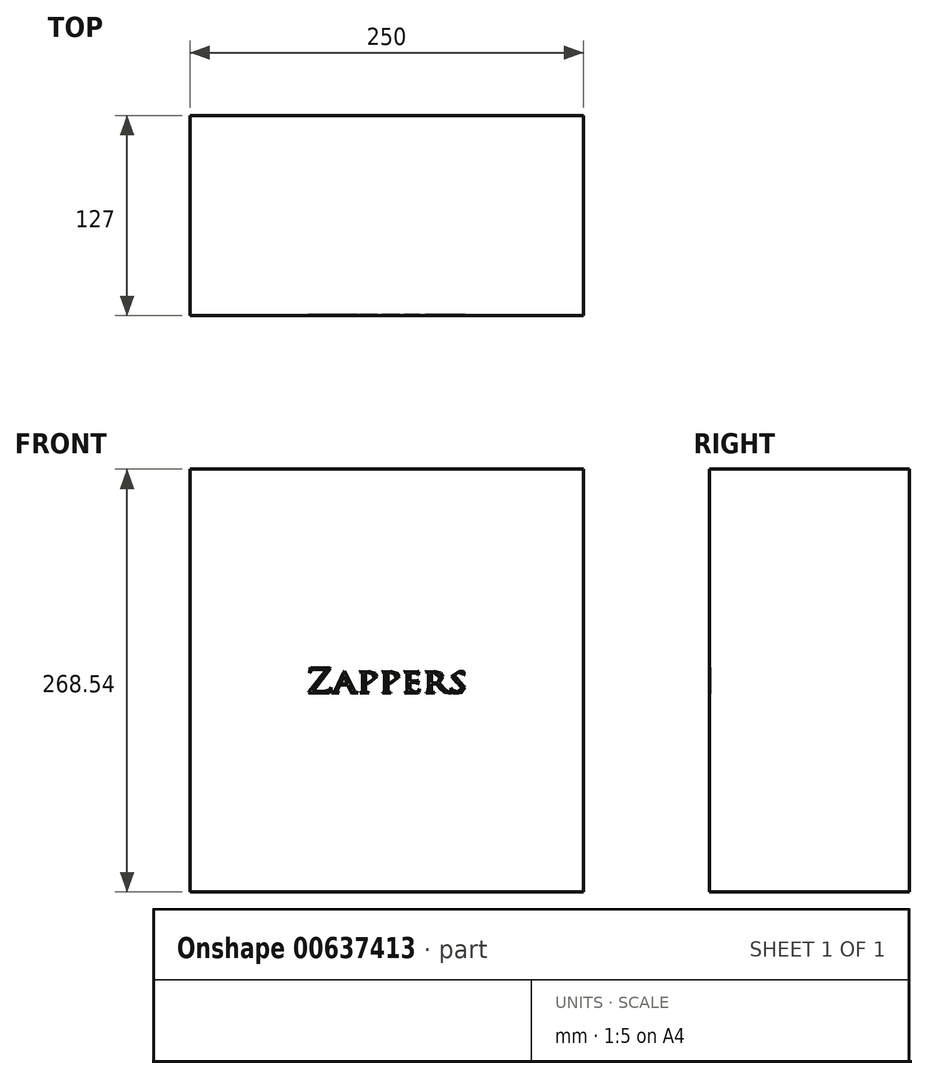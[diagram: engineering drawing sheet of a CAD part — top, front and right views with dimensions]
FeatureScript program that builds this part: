
annotation { "Feature Type Name" : "Feature", "Feature Type Description" : "" }
export const myFeature = defineFeature(function(context is Context, id is Id, definition is map)
    precondition{}
    {
        {
            var Q0;
            Q0=qCreatedBy(makeId("Front.planeOp"),FACE);
            var sketch = newSketch(context, id + "F0", { "sketchPlane" : qUnion([Q0])});
            skLineSegment(sketch, "E0.bottom", {"start": v(125, 134.27) * mm, "end": v(-125, 134.27) * mm});
            skLineSegment(sketch, "E0.top", {"start": v(125, -134.27) * mm, "end": v(-125, -134.27) * mm});
            skLineSegment(sketch, "E0.left", {"start": v(125, 134.27) * mm, "end": v(125, -134.27) * mm});
            skLineSegment(sketch, "E0.right", {"start": v(-125, 134.27) * mm, "end": v(-125, -134.27) * mm});
            skPoint(sketch, "E0.middle", {"position": v(0, 0) * mm});
            skSolve(sketch);
        }
        {
            var Q0;
            Q0=makeQuery(id+"F0.imprint","IMPRINT",FACE,{"disambiguationData":[TD([[makeQuery(id+"F0.imprint","IMPRINT",EDGE,{"derivedFrom":sQuery(id+"F0.wireOp",EDGE,"E0.bottom")}),1.0]])]});
            extrude(context, id + "F1", {"entities" : qUnion([Q0]), "endBound" : BoundingType.SYMMETRIC, "depth" : 127 * mm, "offsetDistance" : 25.4 * mm, "hasSecondDirection" : true, "secondDirectionOppositeDirection" : true, "secondDirectionDepth" : 25.4 * mm});
        }
        {
            var Q0;
            Q0=makeQuery(id+"F1.opExtrude","CAP_FACE",FACE,{"disambiguationData":[OSD([sQuery(id+"F0.wireOp",EDGE,"E0.bottom"),sQuery(id+"F0.wireOp",EDGE,"E0.top"),sQuery(id+"F0.wireOp",EDGE,"E0.left"),sQuery(id+"F0.wireOp",EDGE,"E0.right")])],"isStart":false});
            var sketch = newSketch(context, id + "F2", { "sketchPlane" : qUnion([Q0])});
            skLineSegment(sketch, "E1", {"start": v(-40.14, -7) * mm, "end": v(-36.24, -5.97) * mm});
            skLineSegment(sketch, "E2", {"start": v(-36.24, -5.97) * mm, "end": v(-35.75, -4.84) * mm});
            skLineSegment(sketch, "E3", {"start": v(-35.75, -4.84) * mm, "end": v(-35.53, -4.5) * mm});
            skLineSegment(sketch, "E4", {"start": v(-35.53, -4.5) * mm, "end": v(-35.33, -4.98) * mm});
            skLineSegment(sketch, "E5", {"start": v(-35.33, -4.98) * mm, "end": v(-35.82, -7.4) * mm});
            skLineSegment(sketch, "E6", {"start": v(-35.82, -7.4) * mm, "end": v(-36.56, -7.95) * mm});
            skLineSegment(sketch, "E7", {"start": v(-36.56, -7.95) * mm, "end": v(-49.14, -7.84) * mm});
            skLineSegment(sketch, "E8", {"start": v(-49.14, -7.84) * mm, "end": v(-49.58, -7.67) * mm});
            skLineSegment(sketch, "E9", {"start": v(-49.58, -7.67) * mm, "end": v(-49.24, -7.09) * mm});
            skLineSegment(sketch, "E10", {"start": v(-49.24, -7.09) * mm, "end": v(-38.41, 7.13) * mm});
            skLineSegment(sketch, "E11", {"start": v(-38.41, 7.13) * mm, "end": v(-43.76, 7.13) * mm});
            skLineSegment(sketch, "E12", {"start": v(-43.76, 7.13) * mm, "end": v(-47.32, 6.7) * mm});
            skLineSegment(sketch, "E13", {"start": v(-47.32, 6.7) * mm, "end": v(-48.72, 5.05) * mm});
            skLineSegment(sketch, "E14", {"start": v(-48.72, 5.05) * mm, "end": v(-49, 4.67) * mm});
            skLineSegment(sketch, "E15", {"start": v(-49, 4.67) * mm, "end": v(-49.14, 4.94) * mm});
            skLineSegment(sketch, "E16", {"start": v(-49.14, 4.94) * mm, "end": v(-48.65, 7.74) * mm});
            skLineSegment(sketch, "E17", {"start": v(-48.65, 7.74) * mm, "end": v(-48.4, 8.14) * mm});
            skLineSegment(sketch, "E18", {"start": v(-48.4, 8.14) * mm, "end": v(-47.36, 7.99) * mm});
            skLineSegment(sketch, "E19", {"start": v(-47.36, 7.99) * mm, "end": v(-43.07, 7.93) * mm});
            skLineSegment(sketch, "E20", {"start": v(-43.07, 7.93) * mm, "end": v(-36.2, 7.93) * mm});
            skLineSegment(sketch, "E21", {"start": v(-36.2, 7.93) * mm, "end": v(-35.7, 7.76) * mm});
            skLineSegment(sketch, "E22", {"start": v(-35.7, 7.76) * mm, "end": v(-35.8, 7.5) * mm});
            skLineSegment(sketch, "E23", {"start": v(-35.8, 7.5) * mm, "end": v(-46.85, -7) * mm});
            skLineSegment(sketch, "E24", {"start": v(-46.85, -7) * mm, "end": v(-40.14, -7) * mm});
            skLineSegment(sketch, "E25", {"start": v(-27.46, 5.26) * mm, "end": v(-26.94, 5.95) * mm});
            skLineSegment(sketch, "E26", {"start": v(-26.94, 5.95) * mm, "end": v(-26.43, 5.3) * mm});
            skLineSegment(sketch, "E27", {"start": v(-26.43, 5.3) * mm, "end": v(-21.22, -5.55) * mm});
            skLineSegment(sketch, "E28", {"start": v(-21.22, -5.55) * mm, "end": v(-19.37, -7.5) * mm});
            skLineSegment(sketch, "E29", {"start": v(-19.37, -7.5) * mm, "end": v(-18.5, -7.61) * mm});
            skLineSegment(sketch, "E30", {"start": v(-18.5, -7.61) * mm, "end": v(-18.24, -7.76) * mm});
            skLineSegment(sketch, "E31", {"start": v(-18.24, -7.76) * mm, "end": v(-18.73, -7.9) * mm});
            skLineSegment(sketch, "E32", {"start": v(-18.73, -7.9) * mm, "end": v(-22.16, -7.86) * mm});
            skLineSegment(sketch, "E33", {"start": v(-22.16, -7.86) * mm, "end": v(-22.92, -7.74) * mm});
            skLineSegment(sketch, "E34", {"start": v(-22.92, -7.74) * mm, "end": v(-22.78, -7.61) * mm});
            skLineSegment(sketch, "E35", {"start": v(-22.78, -7.61) * mm, "end": v(-22.58, -7.13) * mm});
            skLineSegment(sketch, "E36", {"start": v(-22.58, -7.13) * mm, "end": v(-24.53, -3.03) * mm});
            skLineSegment(sketch, "E37", {"start": v(-24.53, -3.03) * mm, "end": v(-24.72, -2.92) * mm});
            skLineSegment(sketch, "E38", {"start": v(-24.72, -2.92) * mm, "end": v(-29.73, -2.92) * mm});
            skLineSegment(sketch, "E39", {"start": v(-29.73, -2.92) * mm, "end": v(-29.95, -3.07) * mm});
            skLineSegment(sketch, "E40", {"start": v(-29.95, -3.07) * mm, "end": v(-31.19, -5.93) * mm});
            skLineSegment(sketch, "E41", {"start": v(-31.19, -5.93) * mm, "end": v(-31.5, -7.13) * mm});
            skLineSegment(sketch, "E42", {"start": v(-31.5, -7.13) * mm, "end": v(-30.77, -7.61) * mm});
            skLineSegment(sketch, "E43", {"start": v(-30.77, -7.61) * mm, "end": v(-30.57, -7.61) * mm});
            skLineSegment(sketch, "E44", {"start": v(-30.57, -7.61) * mm, "end": v(-30.35, -7.76) * mm});
            skLineSegment(sketch, "E45", {"start": v(-30.35, -7.76) * mm, "end": v(-30.67, -7.9) * mm});
            skLineSegment(sketch, "E46", {"start": v(-30.67, -7.9) * mm, "end": v(-32.62, -7.84) * mm});
            skLineSegment(sketch, "E47", {"start": v(-32.62, -7.84) * mm, "end": v(-34.81, -7.9) * mm});
            skLineSegment(sketch, "E48", {"start": v(-34.81, -7.9) * mm, "end": v(-35.23, -7.76) * mm});
            skLineSegment(sketch, "E49", {"start": v(-35.23, -7.76) * mm, "end": v(-35.03, -7.61) * mm});
            skLineSegment(sketch, "E50", {"start": v(-35.03, -7.61) * mm, "end": v(-34.4, -7.57) * mm});
            skLineSegment(sketch, "E51", {"start": v(-34.4, -7.57) * mm, "end": v(-32.57, -5.93) * mm});
            skLineSegment(sketch, "E52", {"start": v(-32.57, -5.93) * mm, "end": v(-27.46, 5.26) * mm});
            skLineSegment(sketch, "E53", {"start": v(-25.04, -2.19) * mm, "end": v(-24.97, -2.06) * mm});
            skLineSegment(sketch, "E54", {"start": v(-24.97, -2.06) * mm, "end": v(-27.12, 2.84) * mm});
            skLineSegment(sketch, "E55", {"start": v(-27.12, 2.84) * mm, "end": v(-27.49, 2.84) * mm});
            skLineSegment(sketch, "E56", {"start": v(-27.49, 2.84) * mm, "end": v(-29.5, -2.06) * mm});
            skLineSegment(sketch, "E57", {"start": v(-29.5, -2.06) * mm, "end": v(-29.43, -2.19) * mm});
            skLineSegment(sketch, "E58", {"start": v(-29.43, -2.19) * mm, "end": v(-25.04, -2.19) * mm});
            skLineSegment(sketch, "E59", {"start": v(-15.38, 0.44) * mm, "end": v(-15.43, 4.29) * mm});
            skLineSegment(sketch, "E60", {"start": v(-15.43, 4.29) * mm, "end": v(-16.31, 5.28) * mm});
            skLineSegment(sketch, "E61", {"start": v(-16.31, 5.28) * mm, "end": v(-17.05, 5.32) * mm});
            skLineSegment(sketch, "E62", {"start": v(-17.05, 5.32) * mm, "end": v(-17.23, 5.47) * mm});
            skLineSegment(sketch, "E63", {"start": v(-17.23, 5.47) * mm, "end": v(-16.88, 5.61) * mm});
            skLineSegment(sketch, "E64", {"start": v(-16.88, 5.61) * mm, "end": v(-14.37, 5.57) * mm});
            skLineSegment(sketch, "E65", {"start": v(-14.37, 5.57) * mm, "end": v(-11.28, 5.61) * mm});
            skLineSegment(sketch, "E66", {"start": v(-11.28, 5.61) * mm, "end": v(-7.14, 4.6) * mm});
            skLineSegment(sketch, "E67", {"start": v(-7.14, 4.6) * mm, "end": v(-6.05, 2.46) * mm});
            skLineSegment(sketch, "E68", {"start": v(-6.05, 2.46) * mm, "end": v(-11.65, -1.8) * mm});
            skLineSegment(sketch, "E69", {"start": v(-11.65, -1.8) * mm, "end": v(-12.27, -1.79) * mm});
            skLineSegment(sketch, "E70", {"start": v(-12.27, -1.79) * mm, "end": v(-12.5, -1.62) * mm});
            skLineSegment(sketch, "E71", {"start": v(-12.5, -1.62) * mm, "end": v(-11.92, -1.43) * mm});
            skLineSegment(sketch, "E72", {"start": v(-11.92, -1.43) * mm, "end": v(-7.9, 1.45) * mm});
            skLineSegment(sketch, "E73", {"start": v(-7.9, 1.45) * mm, "end": v(-9.14, 4.16) * mm});
            skLineSegment(sketch, "E74", {"start": v(-9.14, 4.16) * mm, "end": v(-12.07, 5.03) * mm});
            skLineSegment(sketch, "E75", {"start": v(-12.07, 5.03) * mm, "end": v(-13.28, 4.9) * mm});
            skLineSegment(sketch, "E76", {"start": v(-13.28, 4.9) * mm, "end": v(-13.45, 4.56) * mm});
            skLineSegment(sketch, "E77", {"start": v(-13.45, 4.56) * mm, "end": v(-13.45, -2.71) * mm});
            skLineSegment(sketch, "E78", {"start": v(-13.45, -2.71) * mm, "end": v(-13.36, -6.58) * mm});
            skLineSegment(sketch, "E79", {"start": v(-13.36, -6.58) * mm, "end": v(-12.5, -7.53) * mm});
            skLineSegment(sketch, "E80", {"start": v(-12.5, -7.53) * mm, "end": v(-11.53, -7.61) * mm});
            skLineSegment(sketch, "E81", {"start": v(-11.53, -7.61) * mm, "end": v(-11.36, -7.76) * mm});
            skLineSegment(sketch, "E82", {"start": v(-11.36, -7.76) * mm, "end": v(-11.7, -7.9) * mm});
            skLineSegment(sketch, "E83", {"start": v(-11.7, -7.9) * mm, "end": v(-14.42, -7.84) * mm});
            skLineSegment(sketch, "E84", {"start": v(-14.42, -7.84) * mm, "end": v(-16.56, -7.9) * mm});
            skLineSegment(sketch, "E85", {"start": v(-16.56, -7.9) * mm, "end": v(-16.9, -7.76) * mm});
            skLineSegment(sketch, "E86", {"start": v(-16.9, -7.76) * mm, "end": v(-16.73, -7.61) * mm});
            skLineSegment(sketch, "E87", {"start": v(-16.73, -7.61) * mm, "end": v(-16.07, -7.53) * mm});
            skLineSegment(sketch, "E88", {"start": v(-16.07, -7.53) * mm, "end": v(-15.5, -6.58) * mm});
            skLineSegment(sketch, "E89", {"start": v(-15.5, -6.58) * mm, "end": v(-15.38, -2.71) * mm});
            skLineSegment(sketch, "E90", {"start": v(-15.38, -2.71) * mm, "end": v(-15.38, 0.44) * mm});
            skLineSegment(sketch, "E91", {"start": v(-1.27, 0.44) * mm, "end": v(-1.32, 4.29) * mm});
            skLineSegment(sketch, "E92", {"start": v(-1.32, 4.29) * mm, "end": v(-2.2, 5.28) * mm});
            skLineSegment(sketch, "E93", {"start": v(-2.2, 5.28) * mm, "end": v(-2.95, 5.32) * mm});
            skLineSegment(sketch, "E94", {"start": v(-2.95, 5.32) * mm, "end": v(-3.12, 5.47) * mm});
            skLineSegment(sketch, "E95", {"start": v(-3.12, 5.47) * mm, "end": v(-2.78, 5.61) * mm});
            skLineSegment(sketch, "E96", {"start": v(-2.78, 5.61) * mm, "end": v(-0.26, 5.57) * mm});
            skLineSegment(sketch, "E97", {"start": v(-0.26, 5.57) * mm, "end": v(2.82, 5.61) * mm});
            skLineSegment(sketch, "E98", {"start": v(2.82, 5.61) * mm, "end": v(6.97, 4.6) * mm});
            skLineSegment(sketch, "E99", {"start": v(6.97, 4.6) * mm, "end": v(8.05, 2.46) * mm});
            skLineSegment(sketch, "E100", {"start": v(8.05, 2.46) * mm, "end": v(2.45, -1.8) * mm});
            skLineSegment(sketch, "E101", {"start": v(2.45, -1.8) * mm, "end": v(1.84, -1.79) * mm});
            skLineSegment(sketch, "E102", {"start": v(1.84, -1.79) * mm, "end": v(1.62, -1.62) * mm});
            skLineSegment(sketch, "E103", {"start": v(1.62, -1.62) * mm, "end": v(2.18, -1.43) * mm});
            skLineSegment(sketch, "E104", {"start": v(2.18, -1.43) * mm, "end": v(6.2, 1.45) * mm});
            skLineSegment(sketch, "E105", {"start": v(6.2, 1.45) * mm, "end": v(4.97, 4.16) * mm});
            skLineSegment(sketch, "E106", {"start": v(4.97, 4.16) * mm, "end": v(2.03, 5.03) * mm});
            skLineSegment(sketch, "E107", {"start": v(2.03, 5.03) * mm, "end": v(0.83, 4.9) * mm});
            skLineSegment(sketch, "E108", {"start": v(0.83, 4.9) * mm, "end": v(0.65, 4.56) * mm});
            skLineSegment(sketch, "E109", {"start": v(0.65, 4.56) * mm, "end": v(0.65, -2.71) * mm});
            skLineSegment(sketch, "E110", {"start": v(0.65, -2.71) * mm, "end": v(0.75, -6.58) * mm});
            skLineSegment(sketch, "E111", {"start": v(0.75, -6.58) * mm, "end": v(1.62, -7.53) * mm});
            skLineSegment(sketch, "E112", {"start": v(1.62, -7.53) * mm, "end": v(2.58, -7.61) * mm});
            skLineSegment(sketch, "E113", {"start": v(2.58, -7.61) * mm, "end": v(2.75, -7.76) * mm});
            skLineSegment(sketch, "E114", {"start": v(2.75, -7.76) * mm, "end": v(2.4, -7.9) * mm});
            skLineSegment(sketch, "E115", {"start": v(2.4, -7.9) * mm, "end": v(-0.3, -7.84) * mm});
            skLineSegment(sketch, "E116", {"start": v(-0.3, -7.84) * mm, "end": v(-2.45, -7.9) * mm});
            skLineSegment(sketch, "E117", {"start": v(-2.45, -7.9) * mm, "end": v(-2.8, -7.76) * mm});
            skLineSegment(sketch, "E118", {"start": v(-2.8, -7.76) * mm, "end": v(-2.63, -7.61) * mm});
            skLineSegment(sketch, "E119", {"start": v(-2.63, -7.61) * mm, "end": v(-1.96, -7.53) * mm});
            skLineSegment(sketch, "E120", {"start": v(-1.96, -7.53) * mm, "end": v(-1.4, -6.58) * mm});
            skLineSegment(sketch, "E121", {"start": v(-1.4, -6.58) * mm, "end": v(-1.27, -2.71) * mm});
            skLineSegment(sketch, "E122", {"start": v(-1.27, -2.71) * mm, "end": v(-1.27, 0.44) * mm});
            skLineSegment(sketch, "E123", {"start": v(12.84, 0.44) * mm, "end": v(12.79, 4.29) * mm});
            skLineSegment(sketch, "E124", {"start": v(12.79, 4.29) * mm, "end": v(11.9, 5.28) * mm});
            skLineSegment(sketch, "E125", {"start": v(11.9, 5.28) * mm, "end": v(11.16, 5.32) * mm});
            skLineSegment(sketch, "E126", {"start": v(11.16, 5.32) * mm, "end": v(10.99, 5.47) * mm});
            skLineSegment(sketch, "E127", {"start": v(10.99, 5.47) * mm, "end": v(11.33, 5.61) * mm});
            skLineSegment(sketch, "E128", {"start": v(11.33, 5.61) * mm, "end": v(13.85, 5.57) * mm});
            skLineSegment(sketch, "E129", {"start": v(13.85, 5.57) * mm, "end": v(19.03, 5.57) * mm});
            skLineSegment(sketch, "E130", {"start": v(19.03, 5.57) * mm, "end": v(20.01, 5.68) * mm});
            skLineSegment(sketch, "E131", {"start": v(20.01, 5.68) * mm, "end": v(20.31, 5.76) * mm});
            skLineSegment(sketch, "E132", {"start": v(20.31, 5.76) * mm, "end": v(20.4, 5.6) * mm});
            skLineSegment(sketch, "E133", {"start": v(20.4, 5.6) * mm, "end": v(20.24, 4.75) * mm});
            skLineSegment(sketch, "E134", {"start": v(20.24, 4.75) * mm, "end": v(20.11, 3.57) * mm});
            skLineSegment(sketch, "E135", {"start": v(20.11, 3.57) * mm, "end": v(19.92, 3.38) * mm});
            skLineSegment(sketch, "E136", {"start": v(19.92, 3.38) * mm, "end": v(19.74, 3.62) * mm});
            skLineSegment(sketch, "E137", {"start": v(19.74, 3.62) * mm, "end": v(19.62, 4.25) * mm});
            skLineSegment(sketch, "E138", {"start": v(19.62, 4.25) * mm, "end": v(18.07, 4.8) * mm});
            skLineSegment(sketch, "E139", {"start": v(18.07, 4.8) * mm, "end": v(14.93, 4.86) * mm});
            skLineSegment(sketch, "E140", {"start": v(14.93, 4.86) * mm, "end": v(14.81, 4.67) * mm});
            skLineSegment(sketch, "E141", {"start": v(14.81, 4.67) * mm, "end": v(14.81, -0.19) * mm});
            skLineSegment(sketch, "E142", {"start": v(14.81, -0.19) * mm, "end": v(14.93, -0.38) * mm});
            skLineSegment(sketch, "E143", {"start": v(14.93, -0.38) * mm, "end": v(18.56, -0.34) * mm});
            skLineSegment(sketch, "E144", {"start": v(18.56, -0.34) * mm, "end": v(19.62, -0.08) * mm});
            skLineSegment(sketch, "E145", {"start": v(19.62, -0.08) * mm, "end": v(19.94, 0.15) * mm});
            skLineSegment(sketch, "E146", {"start": v(19.94, 0.15) * mm, "end": v(20.06, 0) * mm});
            skLineSegment(sketch, "E147", {"start": v(20.06, 0) * mm, "end": v(19.9, -0.99) * mm});
            skLineSegment(sketch, "E148", {"start": v(19.9, -0.99) * mm, "end": v(19.8, -2.14) * mm});
            skLineSegment(sketch, "E149", {"start": v(19.8, -2.14) * mm, "end": v(19.6, -2.48) * mm});
            skLineSegment(sketch, "E150", {"start": v(19.6, -2.48) * mm, "end": v(19.45, -2.31) * mm});
            skLineSegment(sketch, "E151", {"start": v(19.45, -2.31) * mm, "end": v(19.35, -1.72) * mm});
            skLineSegment(sketch, "E152", {"start": v(19.35, -1.72) * mm, "end": v(18.24, -1.18) * mm});
            skLineSegment(sketch, "E153", {"start": v(18.24, -1.18) * mm, "end": v(14.96, -1.1) * mm});
            skLineSegment(sketch, "E154", {"start": v(14.96, -1.1) * mm, "end": v(14.81, -1.22) * mm});
            skLineSegment(sketch, "E155", {"start": v(14.81, -1.22) * mm, "end": v(14.81, -2.71) * mm});
            skLineSegment(sketch, "E156", {"start": v(14.81, -2.71) * mm, "end": v(14.81, -5.76) * mm});
            skLineSegment(sketch, "E157", {"start": v(14.81, -5.76) * mm, "end": v(17.4, -7.2) * mm});
            skLineSegment(sketch, "E158", {"start": v(17.4, -7.2) * mm, "end": v(19.57, -7) * mm});
            skLineSegment(sketch, "E159", {"start": v(19.57, -7) * mm, "end": v(20.56, -5.76) * mm});
            skLineSegment(sketch, "E160", {"start": v(20.56, -5.76) * mm, "end": v(20.78, -5.49) * mm});
            skLineSegment(sketch, "E161", {"start": v(20.78, -5.49) * mm, "end": v(20.93, -5.76) * mm});
            skLineSegment(sketch, "E162", {"start": v(20.93, -5.76) * mm, "end": v(20.63, -7.49) * mm});
            skLineSegment(sketch, "E163", {"start": v(20.63, -7.49) * mm, "end": v(19.42, -7.95) * mm});
            skLineSegment(sketch, "E164", {"start": v(19.42, -7.95) * mm, "end": v(15.65, -7.88) * mm});
            skLineSegment(sketch, "E165", {"start": v(15.65, -7.88) * mm, "end": v(13.85, -7.84) * mm});
            skLineSegment(sketch, "E166", {"start": v(13.85, -7.84) * mm, "end": v(12.91, -7.86) * mm});
            skLineSegment(sketch, "E167", {"start": v(12.91, -7.86) * mm, "end": v(11.65, -7.9) * mm});
            skLineSegment(sketch, "E168", {"start": v(11.65, -7.9) * mm, "end": v(11.3, -7.76) * mm});
            skLineSegment(sketch, "E169", {"start": v(11.3, -7.76) * mm, "end": v(11.48, -7.61) * mm});
            skLineSegment(sketch, "E170", {"start": v(11.48, -7.61) * mm, "end": v(12.15, -7.53) * mm});
            skLineSegment(sketch, "E171", {"start": v(12.15, -7.53) * mm, "end": v(12.71, -6.58) * mm});
            skLineSegment(sketch, "E172", {"start": v(12.71, -6.58) * mm, "end": v(12.84, -2.71) * mm});
            skLineSegment(sketch, "E173", {"start": v(12.84, -2.71) * mm, "end": v(12.84, 0.44) * mm});
            skLineSegment(sketch, "E174", {"start": v(26.43, 0.44) * mm, "end": v(26.38, 4.29) * mm});
            skLineSegment(sketch, "E175", {"start": v(26.38, 4.29) * mm, "end": v(25.49, 5.28) * mm});
            skLineSegment(sketch, "E176", {"start": v(25.49, 5.28) * mm, "end": v(24.75, 5.32) * mm});
            skLineSegment(sketch, "E177", {"start": v(24.75, 5.32) * mm, "end": v(24.58, 5.47) * mm});
            skLineSegment(sketch, "E178", {"start": v(24.58, 5.47) * mm, "end": v(24.92, 5.61) * mm});
            skLineSegment(sketch, "E179", {"start": v(24.92, 5.61) * mm, "end": v(27.49, 5.57) * mm});
            skLineSegment(sketch, "E180", {"start": v(27.49, 5.57) * mm, "end": v(30.2, 5.61) * mm});
            skLineSegment(sketch, "E181", {"start": v(30.2, 5.61) * mm, "end": v(34.24, 4.84) * mm});
            skLineSegment(sketch, "E182", {"start": v(34.24, 4.84) * mm, "end": v(35.75, 2.4) * mm});
            skLineSegment(sketch, "E183", {"start": v(35.75, 2.4) * mm, "end": v(33.08, -1.68) * mm});
            skLineSegment(sketch, "E184", {"start": v(33.08, -1.68) * mm, "end": v(37.62, -6.3) * mm});
            skLineSegment(sketch, "E185", {"start": v(37.62, -6.3) * mm, "end": v(40.04, -7.55) * mm});
            skLineSegment(sketch, "E186", {"start": v(40.04, -7.55) * mm, "end": v(40.8, -7.61) * mm});
            skLineSegment(sketch, "E187", {"start": v(40.8, -7.61) * mm, "end": v(41, -7.76) * mm});
            skLineSegment(sketch, "E188", {"start": v(41, -7.76) * mm, "end": v(40.48, -7.9) * mm});
            skLineSegment(sketch, "E189", {"start": v(40.48, -7.9) * mm, "end": v(39.13, -7.9) * mm});
            skLineSegment(sketch, "E190", {"start": v(39.13, -7.9) * mm, "end": v(36.8, -7.55) * mm});
            skLineSegment(sketch, "E191", {"start": v(36.8, -7.55) * mm, "end": v(33.85, -4.92) * mm});
            skLineSegment(sketch, "E192", {"start": v(33.85, -4.92) * mm, "end": v(31.5, -2.31) * mm});
            skLineSegment(sketch, "E193", {"start": v(31.5, -2.31) * mm, "end": v(31.21, -2.2) * mm});
            skLineSegment(sketch, "E194", {"start": v(31.21, -2.2) * mm, "end": v(28.45, -2.17) * mm});
            skLineSegment(sketch, "E195", {"start": v(28.45, -2.17) * mm, "end": v(28.3, -2.31) * mm});
            skLineSegment(sketch, "E196", {"start": v(28.3, -2.31) * mm, "end": v(28.3, -2.73) * mm});
            skLineSegment(sketch, "E197", {"start": v(28.3, -2.73) * mm, "end": v(28.4, -6.58) * mm});
            skLineSegment(sketch, "E198", {"start": v(28.4, -6.58) * mm, "end": v(29.26, -7.53) * mm});
            skLineSegment(sketch, "E199", {"start": v(29.26, -7.53) * mm, "end": v(30.22, -7.61) * mm});
            skLineSegment(sketch, "E200", {"start": v(30.22, -7.61) * mm, "end": v(30.4, -7.76) * mm});
            skLineSegment(sketch, "E201", {"start": v(30.4, -7.76) * mm, "end": v(30.05, -7.9) * mm});
            skLineSegment(sketch, "E202", {"start": v(30.05, -7.9) * mm, "end": v(27.39, -7.84) * mm});
            skLineSegment(sketch, "E203", {"start": v(27.39, -7.84) * mm, "end": v(25.24, -7.9) * mm});
            skLineSegment(sketch, "E204", {"start": v(25.24, -7.9) * mm, "end": v(24.9, -7.76) * mm});
            skLineSegment(sketch, "E205", {"start": v(24.9, -7.76) * mm, "end": v(25.07, -7.61) * mm});
            skLineSegment(sketch, "E206", {"start": v(25.07, -7.61) * mm, "end": v(25.73, -7.53) * mm});
            skLineSegment(sketch, "E207", {"start": v(25.73, -7.53) * mm, "end": v(26.3, -6.58) * mm});
            skLineSegment(sketch, "E208", {"start": v(26.3, -6.58) * mm, "end": v(26.43, -2.71) * mm});
            skLineSegment(sketch, "E209", {"start": v(26.43, -2.71) * mm, "end": v(26.43, 0.44) * mm});
            skLineSegment(sketch, "E210", {"start": v(28.3, -1.07) * mm, "end": v(28.45, -1.3) * mm});
            skLineSegment(sketch, "E211", {"start": v(28.45, -1.3) * mm, "end": v(30.84, -1.58) * mm});
            skLineSegment(sketch, "E212", {"start": v(30.84, -1.58) * mm, "end": v(32.47, -1.26) * mm});
            skLineSegment(sketch, "E213", {"start": v(32.47, -1.26) * mm, "end": v(33.78, 1.47) * mm});
            skLineSegment(sketch, "E214", {"start": v(33.78, 1.47) * mm, "end": v(30.03, 4.98) * mm});
            skLineSegment(sketch, "E215", {"start": v(30.03, 4.98) * mm, "end": v(28.47, 4.88) * mm});
            skLineSegment(sketch, "E216", {"start": v(28.47, 4.88) * mm, "end": v(28.3, 4.67) * mm});
            skLineSegment(sketch, "E217", {"start": v(28.3, 4.67) * mm, "end": v(28.3, -1.07) * mm});
            skLineSegment(sketch, "E218", {"start": v(40.95, -7.65) * mm, "end": v(40.63, -6.98) * mm});
            skLineSegment(sketch, "E219", {"start": v(40.63, -6.98) * mm, "end": v(40.75, -5.09) * mm});
            skLineSegment(sketch, "E220", {"start": v(40.75, -5.09) * mm, "end": v(40.93, -4.8) * mm});
            skLineSegment(sketch, "E221", {"start": v(40.93, -4.8) * mm, "end": v(41.12, -5) * mm});
            skLineSegment(sketch, "E222", {"start": v(41.12, -5) * mm, "end": v(41.2, -5.66) * mm});
            skLineSegment(sketch, "E223", {"start": v(41.2, -5.66) * mm, "end": v(44.63, -7.42) * mm});
            skLineSegment(sketch, "E224", {"start": v(44.63, -7.42) * mm, "end": v(47.88, -5.05) * mm});
            skLineSegment(sketch, "E225", {"start": v(47.88, -5.05) * mm, "end": v(45.14, -1.93) * mm});
            skLineSegment(sketch, "E226", {"start": v(45.14, -1.93) * mm, "end": v(44.16, -1.3) * mm});
            skLineSegment(sketch, "E227", {"start": v(44.16, -1.3) * mm, "end": v(41.05, 2.52) * mm});
            skLineSegment(sketch, "E228", {"start": v(41.05, 2.52) * mm, "end": v(45.86, 5.89) * mm});
            skLineSegment(sketch, "E229", {"start": v(45.86, 5.89) * mm, "end": v(48.1, 5.68) * mm});
            skLineSegment(sketch, "E230", {"start": v(48.1, 5.68) * mm, "end": v(48.87, 5.6) * mm});
            skLineSegment(sketch, "E231", {"start": v(48.87, 5.6) * mm, "end": v(49.1, 5.47) * mm});
            skLineSegment(sketch, "E232", {"start": v(49.1, 5.47) * mm, "end": v(49, 3.57) * mm});
            skLineSegment(sketch, "E233", {"start": v(49, 3.57) * mm, "end": v(48.82, 3.17) * mm});
            skLineSegment(sketch, "E234", {"start": v(48.82, 3.17) * mm, "end": v(48.62, 3.4) * mm});
            skLineSegment(sketch, "E235", {"start": v(48.62, 3.4) * mm, "end": v(48.3, 4.29) * mm});
            skLineSegment(sketch, "E236", {"start": v(48.3, 4.29) * mm, "end": v(45.5, 5.17) * mm});
            skLineSegment(sketch, "E237", {"start": v(45.5, 5.17) * mm, "end": v(42.6, 3.24) * mm});
            skLineSegment(sketch, "E238", {"start": v(42.6, 3.24) * mm, "end": v(45.42, 0.21) * mm});
            skLineSegment(sketch, "E239", {"start": v(45.42, 0.21) * mm, "end": v(46.03, -0.15) * mm});
            skLineSegment(sketch, "E240", {"start": v(46.03, -0.15) * mm, "end": v(49.58, -4.46) * mm});
            skLineSegment(sketch, "E241", {"start": v(49.58, -4.46) * mm, "end": v(47.56, -7.5) * mm});
            skLineSegment(sketch, "E242", {"start": v(47.56, -7.5) * mm, "end": v(44.1, -8.14) * mm});
            skLineSegment(sketch, "E243", {"start": v(44.1, -8.14) * mm, "end": v(40.95, -7.65) * mm});
            skSolve(sketch);
        }
        {
            var Q0;
            Q0 = qSketchRegion(id + "F2", true);
            extrude(context, id + "F3", {"entities" : qUnion([Q0]), "operationType" : NewBodyOperationType.REMOVE, "oppositeDirection" : true, "depth" : 0.5 * mm, "offsetDistance" : 25.4 * mm});
        }
    });
